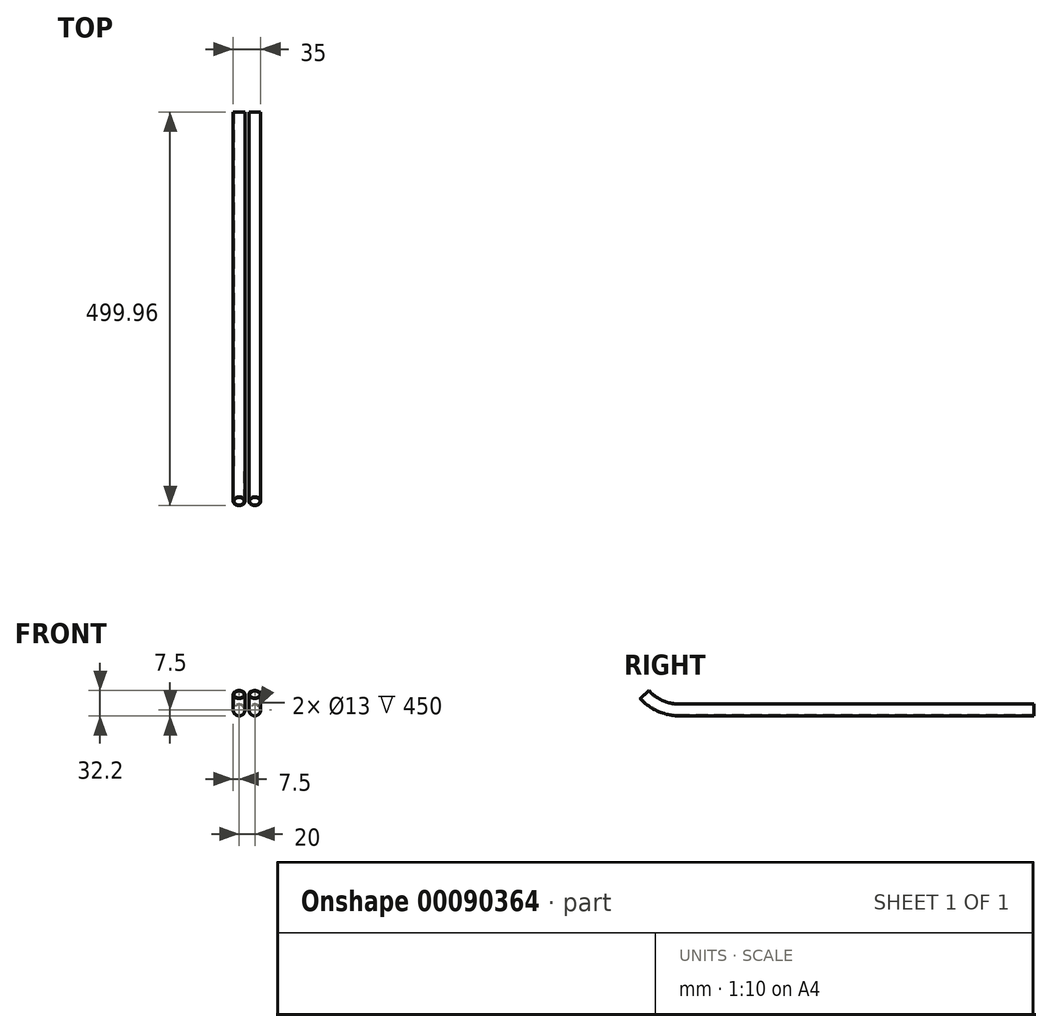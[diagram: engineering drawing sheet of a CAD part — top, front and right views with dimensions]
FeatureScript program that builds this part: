
annotation { "Feature Type Name" : "Feature", "Feature Type Description" : "" }
export const myFeature = defineFeature(function(context is Context, id is Id, definition is map)
    precondition{}
    {
        {
            var Q0;
            Q0=qCreatedBy(makeId("Front.planeOp"),FACE);
            var sketch = newSketch(context, id + "F0", { "sketchPlane" : qUnion([Q0])});
            skCircle(sketch, "E0", {"center": v(0, 0) * mm, "radius": 7.5 * mm});
            skCircle(sketch, "E1.0", {"center": v(0, 0) * mm, "radius": 6.5 * mm});
            skSolve(sketch);
        }
        {
            var Q0;
            Q0=qCreatedBy(makeId("Right.planeOp"),FACE);
            var sketch = newSketch(context, id + "F1", { "sketchPlane" : qUnion([Q0])});
            skLineSegment(sketch, "E2", {"start": v(0, 0) * mm, "end": v(-450, 0) * mm});
            skArc(sketch, "E3", {"start": v(-450, 0) * mm, "mid": v(-474.28, 5.13) * mm, "end": v(-494.41, 19.66) * mm});
            skSolve(sketch);
        }
        {
            var Q0;
            Q0=makeQuery(id+"F0.imprint","IMPRINT",FACE,{"disambiguationData":[TD([[makeQuery(id+"F0.imprint","IMPRINT",EDGE,{"derivedFrom":sQuery(id+"F0.wireOp",EDGE,"E0")}),1.0]])]});
            var Q1;
            Q1=sQuery(id+"F1.wireOp",EDGE,"E2");
            var Q2;
            Q2=sQuery(id+"F1.wireOp",EDGE,"E3");
            sweep(context, id + "F2", {"profiles" : qUnion([Q0]), "path" : qUnion([Q1, Q2])});
        }
        {
            var Q0;
            Q0=qCreatedBy(makeId("Top.planeOp"),FACE);
            var sketch = newSketch(context, id + "F3", { "sketchPlane" : qUnion([Q0])});
            skLineSegment(sketch, "E4.bottom", {"start": v(-18.32, 92.08) * mm, "end": v(-102.1, 92.08) * mm});
            skLineSegment(sketch, "E4.top", {"start": v(-18.32, -31.78) * mm, "end": v(-102.1, -31.78) * mm});
            skLineSegment(sketch, "E4.left", {"start": v(-18.32, 92.08) * mm, "end": v(-18.32, -31.78) * mm});
            skLineSegment(sketch, "E4.right", {"start": v(-102.1, 92.08) * mm, "end": v(-102.1, -31.78) * mm});
            skLineSegment(sketch, "E5", {"start": v(-48.2, 64.04) * mm, "end": v(-48.2, 23.92) * mm});
            skArc(sketch, "E6", {"start": v(-48.2, 23.92) * mm, "mid": v(-63.67, 8.45) * mm, "end": v(-79.14, 23.92) * mm});
            skLineSegment(sketch, "E7", {"start": v(-79.14, 23.92) * mm, "end": v(-79.14, 64.04) * mm});
            skArc(sketch, "E8", {"start": v(-79.14, 64.04) * mm, "mid": v(-63.67, 79.51) * mm, "end": v(-48.2, 64.04) * mm});
            skSolve(sketch);
        }
        {
            var Q0;
            Q0 = qSketchRegion(id + "F3", true);
            var Q1;
            Q1=makeQuery(id+"F3.imprint","IMPRINT",FACE,{"disambiguationData":[TD([[makeQuery(id+"F3.imprint","IMPRINT",EDGE,{"derivedFrom":sQuery(id+"F3.wireOp",EDGE,"E4.bottom")}),1.0]])]});
            extrude(context, id + "F4", {"entities" : qUnion([Q0, Q1]), "depth" : 25 * mm});
        }
        {
            var Q0;
            Q0=makeQuery(id+"F4.opExtrude","SWEPT_BODY",BODY,{"disambiguationData":[OSD([sQuery(id+"F3.wireOp",EDGE,"E4.bottom"),sQuery(id+"F3.wireOp",EDGE,"E4.top"),sQuery(id+"F3.wireOp",EDGE,"E4.left"),sQuery(id+"F3.wireOp",EDGE,"E4.right"),sQuery(id+"F3.wireOp",EDGE,"E5"),sQuery(id+"F3.wireOp",EDGE,"E6"),sQuery(id+"F3.wireOp",EDGE,"E7"),sQuery(id+"F3.wireOp",EDGE,"E8")])]});
            deleteBodies(context, id + "F5", {"entities" : qUnion([Q0])});
        }
        {
            var Q0;
            Q0=makeQuery(id+"F2.opSweep","SWEPT_BODY",BODY,{"disambiguationData":[OSD([sQuery(id+"F0.wireOp",EDGE,"E0"),sQuery(id+"F0.wireOp",EDGE,"E1.0"),sQuery(id+"F1.wireOp",EDGE,"E3")])]});
            transform(context, id + "F6", {"entities" : qUnion([Q0]), "transformType" : TransformType.TRANSLATION_3D, "dx" : 20 * mm, "dy" : 0 * mm, "dz" : 0 * mm, "makeCopy" : true});
        }
    });
